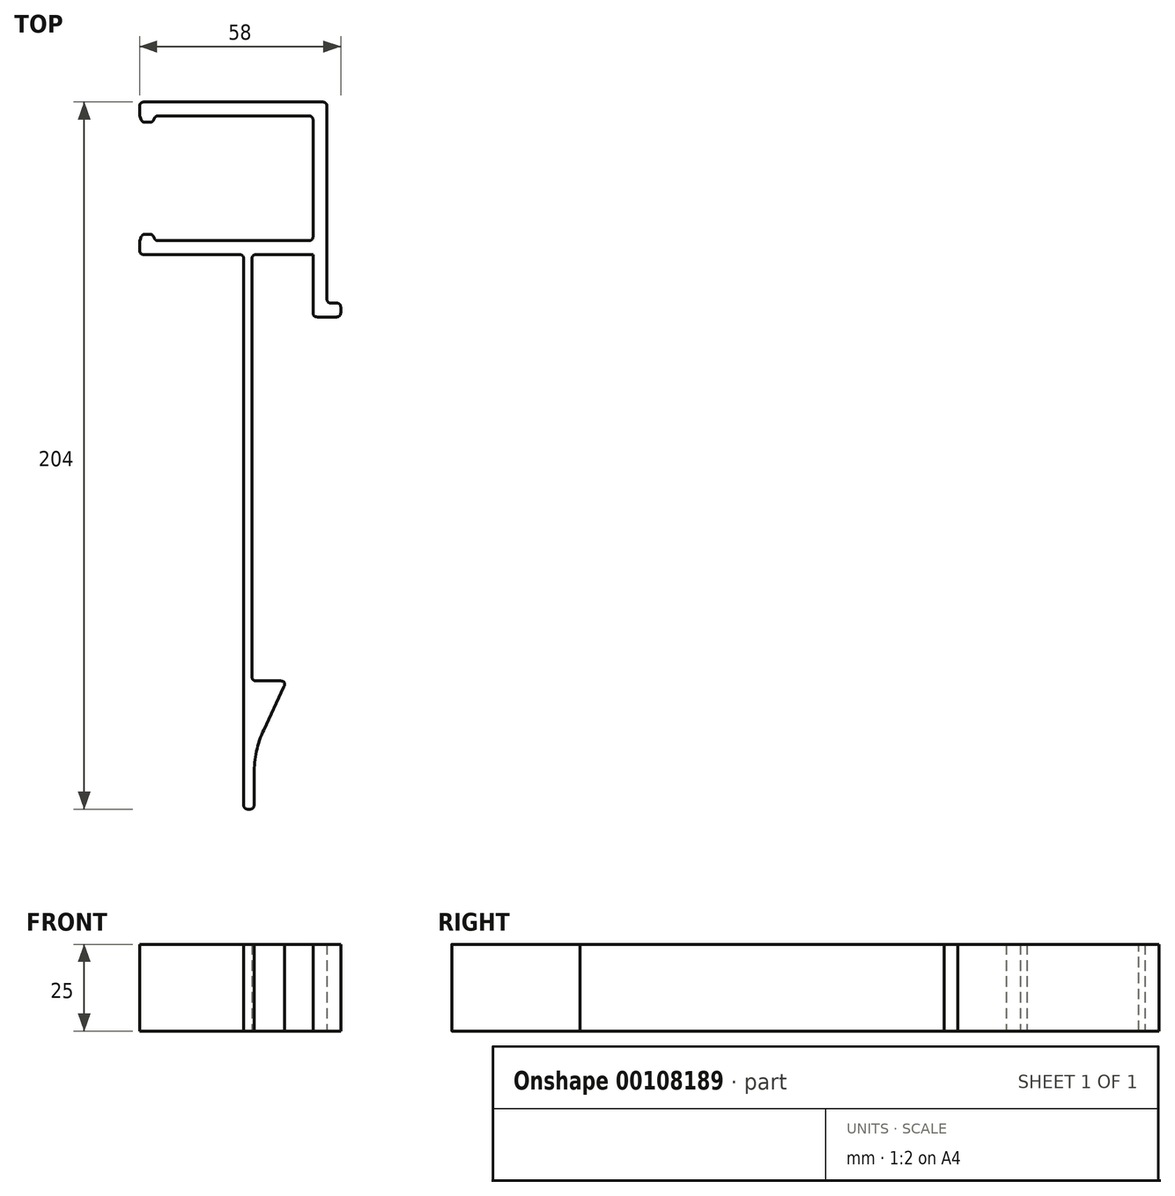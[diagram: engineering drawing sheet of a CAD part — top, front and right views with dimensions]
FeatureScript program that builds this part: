
annotation { "Feature Type Name" : "Feature", "Feature Type Description" : "" }
export const myFeature = defineFeature(function(context is Context, id is Id, definition is map)
    precondition{}
    {
        {
            var Q0;
            Q0=qCreatedBy(makeId("Top.planeOp"),FACE);
            var sketch = newSketch(context, id + "F0", { "sketchPlane" : qUnion([Q0])});
            skLineSegment(sketch, "E0", {"start": v(0, 0) * mm, "end": v(54, 0) * mm});
            skLineSegment(sketch, "E1", {"start": v(54, 0) * mm, "end": v(54, -62) * mm});
            skLineSegment(sketch, "E2", {"start": v(54, -62) * mm, "end": v(50, -62) * mm});
            skLineSegment(sketch, "E3", {"start": v(50, -62) * mm, "end": v(50, -44) * mm});
            skLineSegment(sketch, "E4", {"start": v(50, -44) * mm, "end": v(32.4, -44) * mm});
            skLineSegment(sketch, "E5", {"start": v(32.4, -44) * mm, "end": v(32.4, -167) * mm});
            skLineSegment(sketch, "E6", {"start": v(32.4, -167) * mm, "end": v(42.4, -167) * mm});
            skLineSegment(sketch, "E7", {"start": v(42.4, -167) * mm, "end": v(33, -187.16) * mm});
            skLineSegment(sketch, "E8", {"start": v(33, -187.16) * mm, "end": v(33, -204) * mm});
            skLineSegment(sketch, "E9", {"start": v(33, -204) * mm, "end": v(30, -204) * mm});
            skLineSegment(sketch, "E10", {"start": v(30, -204) * mm, "end": v(30, -44) * mm});
            skLineSegment(sketch, "E11", {"start": v(30, -44) * mm, "end": v(0, -44) * mm});
            skLineSegment(sketch, "E12", {"start": v(0, -44) * mm, "end": v(0, -40) * mm});
            skLineSegment(sketch, "E13", {"start": v(0, -40) * mm, "end": v(50, -40) * mm});
            skLineSegment(sketch, "E14", {"start": v(50, -40) * mm, "end": v(50, -4) * mm});
            skLineSegment(sketch, "E15", {"start": v(50, -4) * mm, "end": v(0, -4) * mm});
            skLineSegment(sketch, "E16", {"start": v(0, -4) * mm, "end": v(0, 0) * mm});
            skLineSegment(sketch, "E17", {"start": v(0, -4) * mm, "end": v(0.75, -5.85) * mm});
            skLineSegment(sketch, "E18", {"start": v(0.75, -5.85) * mm, "end": v(3.75, -5.85) * mm});
            skLineSegment(sketch, "E19", {"start": v(3.75, -5.85) * mm, "end": v(4.5, -4) * mm});
            skLineSegment(sketch, "E20", {"start": v(0, -40) * mm, "end": v(0.75, -38.15) * mm});
            skLineSegment(sketch, "E21", {"start": v(0.75, -38.15) * mm, "end": v(3.75, -38.15) * mm});
            skLineSegment(sketch, "E22", {"start": v(3.75, -38.15) * mm, "end": v(4.5, -40) * mm});
            skLineSegment(sketch, "E23", {"start": v(54, -58) * mm, "end": v(58, -58) * mm});
            skLineSegment(sketch, "E24", {"start": v(58, -58) * mm, "end": v(58, -62) * mm});
            skLineSegment(sketch, "E25", {"start": v(58, -62) * mm, "end": v(54, -62) * mm});
            skSolve(sketch);
        }
        {
            var Q0;
            Q0 = qSketchRegion(id + "F0", true);
            extrude(context, id + "F1", {"entities" : qUnion([Q0]), "depth" : 25 * mm});
        }
        {
            var Q0;
            Q0=makeQuery(id+"F1.opExtrude","SWEPT_EDGE",EDGE,{"disambiguationData":[OSD([sQuery(id+"F0.wireOp",EDGE,"E8"),sQuery(id+"F0.wireOp",EDGE,"E9")])]});
            var Q1;
            Q1=makeQuery(id+"F1.opExtrude","SWEPT_EDGE",EDGE,{"disambiguationData":[OSD([sQuery(id+"F0.wireOp",EDGE,"E9"),sQuery(id+"F0.wireOp",EDGE,"E10")])]});
            var Q2;
            Q2=makeQuery(id+"F1.opExtrude","SWEPT_EDGE",EDGE,{"disambiguationData":[OSD([sQuery(id+"F0.wireOp",EDGE,"E18"),sQuery(id+"F0.wireOp",EDGE,"E19")])]});
            var Q3;
            Q3=makeQuery(id+"F1.opExtrude","SWEPT_EDGE",EDGE,{"disambiguationData":[OSD([sQuery(id+"F0.wireOp",EDGE,"E15"),sQuery(id+"F0.wireOp",EDGE,"E19")])]});
            var Q4;
            Q4=makeQuery(id+"F1.opExtrude","SWEPT_EDGE",EDGE,{"disambiguationData":[OSD([sQuery(id+"F0.wireOp",EDGE,"E17"),sQuery(id+"F0.wireOp",EDGE,"E18")])]});
            var Q5;
            Q5=makeQuery(id+"F1.opExtrude","SWEPT_EDGE",EDGE,{"disambiguationData":[OSD([sQuery(id+"F0.wireOp",EDGE,"E15"),sQuery(id+"F0.wireOp",EDGE,"E16"),sQuery(id+"F0.wireOp",EDGE,"E17")])]});
            var Q6;
            Q6=makeQuery(id+"F1.opExtrude","SWEPT_EDGE",EDGE,{"disambiguationData":[OSD([sQuery(id+"F0.wireOp",EDGE,"E0"),sQuery(id+"F0.wireOp",EDGE,"E16")])]});
            var Q7;
            Q7=makeQuery(id+"F1.opExtrude","SWEPT_EDGE",EDGE,{"disambiguationData":[OSD([sQuery(id+"F0.wireOp",EDGE,"E12"),sQuery(id+"F0.wireOp",EDGE,"E13"),sQuery(id+"F0.wireOp",EDGE,"E20")])]});
            var Q8;
            Q8=makeQuery(id+"F1.opExtrude","SWEPT_EDGE",EDGE,{"disambiguationData":[OSD([sQuery(id+"F0.wireOp",EDGE,"E20"),sQuery(id+"F0.wireOp",EDGE,"E21")])]});
            var Q9;
            Q9=makeQuery(id+"F1.opExtrude","SWEPT_EDGE",EDGE,{"disambiguationData":[OSD([sQuery(id+"F0.wireOp",EDGE,"E11"),sQuery(id+"F0.wireOp",EDGE,"E12")])]});
            var Q10;
            Q10=makeQuery(id+"F1.opExtrude","SWEPT_EDGE",EDGE,{"disambiguationData":[OSD([sQuery(id+"F0.wireOp",EDGE,"E21"),sQuery(id+"F0.wireOp",EDGE,"E22")])]});
            var Q11;
            Q11=makeQuery(id+"F1.opExtrude","SWEPT_EDGE",EDGE,{"disambiguationData":[OSD([sQuery(id+"F0.wireOp",EDGE,"E13"),sQuery(id+"F0.wireOp",EDGE,"E22")])]});
            var Q12;
            Q12=makeQuery(id+"F1.opExtrude","SWEPT_EDGE",EDGE,{"disambiguationData":[OSD([sQuery(id+"F0.wireOp",EDGE,"E13"),sQuery(id+"F0.wireOp",EDGE,"E14")])]});
            var Q13;
            Q13=makeQuery(id+"F1.opExtrude","SWEPT_EDGE",EDGE,{"disambiguationData":[OSD([sQuery(id+"F0.wireOp",EDGE,"E14"),sQuery(id+"F0.wireOp",EDGE,"E15")])]});
            var Q14;
            Q14=makeQuery(id+"F1.opExtrude","SWEPT_EDGE",EDGE,{"disambiguationData":[OSD([sQuery(id+"F0.wireOp",EDGE,"E0"),sQuery(id+"F0.wireOp",EDGE,"E1")])]});
            var Q15;
            Q15=makeQuery(id+"F1.opExtrude","SWEPT_EDGE",EDGE,{"disambiguationData":[OSD([sQuery(id+"F0.wireOp",EDGE,"E23"),sQuery(id+"F0.wireOp",EDGE,"E24")])]});
            var Q16;
            Q16=makeQuery(id+"F1.opExtrude","SWEPT_EDGE",EDGE,{"disambiguationData":[OSD([sQuery(id+"F0.wireOp",EDGE,"E1"),sQuery(id+"F0.wireOp",EDGE,"E23")])]});
            var Q17;
            Q17=makeQuery(id+"F1.opExtrude","SWEPT_EDGE",EDGE,{"disambiguationData":[OSD([sQuery(id+"F0.wireOp",EDGE,"E24"),sQuery(id+"F0.wireOp",EDGE,"E25")])]});
            var Q18;
            Q18=makeQuery(id+"F1.opExtrude","SWEPT_EDGE",EDGE,{"disambiguationData":[OSD([sQuery(id+"F0.wireOp",EDGE,"E2"),sQuery(id+"F0.wireOp",EDGE,"E3")])]});
            var Q19;
            Q19=makeQuery(id+"F1.opExtrude","SWEPT_EDGE",EDGE,{"disambiguationData":[OSD([sQuery(id+"F0.wireOp",EDGE,"E10"),sQuery(id+"F0.wireOp",EDGE,"E11")])]});
            var Q20;
            Q20=makeQuery(id+"F1.opExtrude","SWEPT_EDGE",EDGE,{"disambiguationData":[OSD([sQuery(id+"F0.wireOp",EDGE,"E4"),sQuery(id+"F0.wireOp",EDGE,"E5")])]});
            var Q21;
            Q21=makeQuery(id+"F1.opExtrude","SWEPT_EDGE",EDGE,{"disambiguationData":[OSD([sQuery(id+"F0.wireOp",EDGE,"E6"),sQuery(id+"F0.wireOp",EDGE,"E7")])]});
            var Q22;
            Q22=makeQuery(id+"F1.opExtrude","SWEPT_EDGE",EDGE,{"disambiguationData":[OSD([sQuery(id+"F0.wireOp",EDGE,"E5"),sQuery(id+"F0.wireOp",EDGE,"E6")])]});
            fillet(context, id + "F2", {"entities" : qUnion([Q0, Q1, Q2, Q3, Q4, Q5, Q6, Q7, Q8, Q9, Q10, Q11, Q12, Q13, Q14, Q15, Q16, Q17, Q18, Q19, Q20, Q21, Q22]), "radius" : 1.25 * mm, "tangentPropagation" : true, "rho" : 0.5, "crossSection" : FilletCrossSection.CONIC, "allowEdgeOverflow" : false});
        }
        {
            var Q0;
            Q0=makeQuery(id+"F1.opExtrude","SWEPT_EDGE",EDGE,{"disambiguationData":[OSD([sQuery(id+"F0.wireOp",EDGE,"E7"),sQuery(id+"F0.wireOp",EDGE,"E8")])]});
            fillet(context, id + "F3", {"entities" : qUnion([Q0]), "radius" : 30 * mm, "tangentPropagation" : true, "allowEdgeOverflow" : false});
        }
    });
